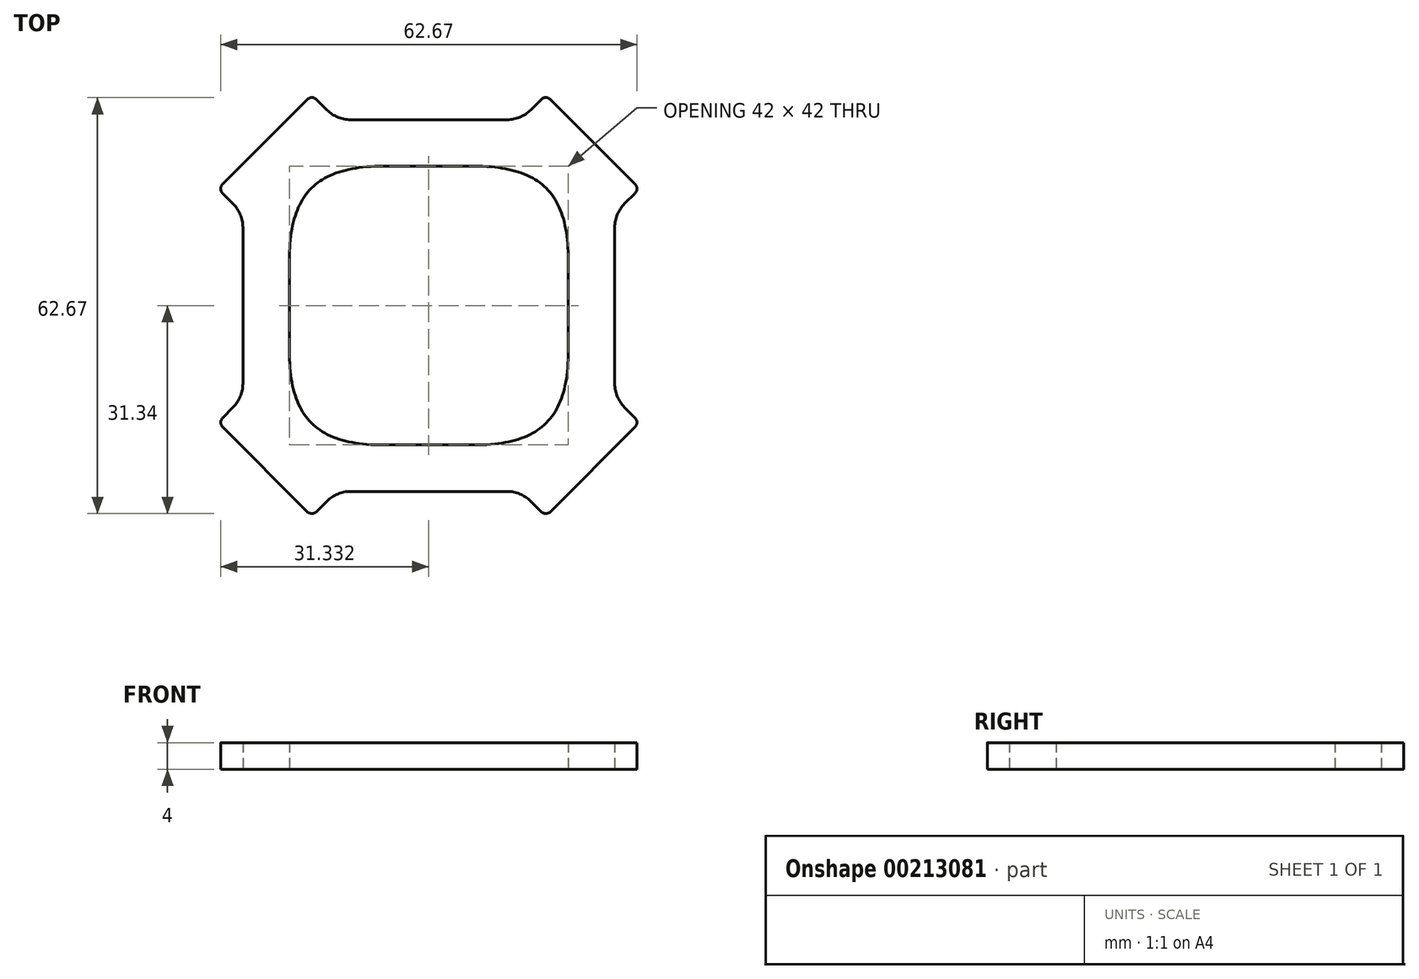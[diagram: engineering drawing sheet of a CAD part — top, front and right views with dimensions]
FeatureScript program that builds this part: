
annotation { "Feature Type Name" : "Feature", "Feature Type Description" : "" }
export const myFeature = defineFeature(function(context is Context, id is Id, definition is map)
    precondition{}
    {
        {
            var Q0;
            Q0=qCreatedBy(makeId("Top.planeOp"),FACE);
            var sketch = newSketch(context, id + "F0", { "sketchPlane" : qUnion([Q0])});
            skLineSegment(sketch, "E0", {"start": v(-155.02, 22.7) * mm, "end": v(-20.02, -112.3) * mm});
            skLineSegment(sketch, "E1", {"start": v(-155.02, -112.3) * mm, "end": v(-20.02, 22.7) * mm});
            skLineSegment(sketch, "E2", {"start": v(-104.42, -13.75) * mm, "end": v(-56.48, -61.69) * mm});
            skLineSegment(sketch, "E3", {"start": v(-118.56, -27.9) * mm, "end": v(-70.62, -75.83) * mm});
            skLineSegment(sketch, "E4", {"start": v(-118.56, -61.69) * mm, "end": v(-70.62, -13.75) * mm});
            skLineSegment(sketch, "E5", {"start": v(-104.42, -75.83) * mm, "end": v(-56.48, -27.9) * mm});
            skLineSegment(sketch, "E6", {"start": v(-115.52, -30.93) * mm, "end": v(-115.52, -58.65) * mm});
            skLineSegment(sketch, "E7", {"start": v(-59.52, -30.93) * mm, "end": v(-59.52, -58.65) * mm});
            skPoint(sketch, "E8", {"position": v(-87.52, -44.8) * mm});
            skCircle(sketch, "E9", {"center": v(-120.52, -33) * mm, "radius": 5 * mm});
            skCircle(sketch, "E10", {"center": v(-120.52, -56.58) * mm, "radius": 5 * mm});
            skCircle(sketch, "E11", {"center": v(-54.52, -33) * mm, "radius": 5 * mm});
            skCircle(sketch, "E12", {"center": v(-54.52, -56.58) * mm, "radius": 5 * mm});
            skLineSegment(sketch, "E13", {"start": v(-101.38, -16.8) * mm, "end": v(-73.66, -16.8) * mm});
            skLineSegment(sketch, "E14", {"start": v(-101.38, -72.8) * mm, "end": v(-73.66, -72.8) * mm});
            skCircle(sketch, "E15", {"center": v(-99.3, -11.8) * mm, "radius": 5 * mm});
            skCircle(sketch, "E16", {"center": v(-75.73, -11.8) * mm, "radius": 5 * mm});
            skCircle(sketch, "E17", {"center": v(-99.3, -77.8) * mm, "radius": 5 * mm});
            skCircle(sketch, "E18", {"center": v(-75.73, -77.8) * mm, "radius": 5 * mm});
            skLineSegment(sketch, "E19", {"start": v(-118.56, -26.48) * mm, "end": v(-105.83, -13.75) * mm});
            skLineSegment(sketch, "E20", {"start": v(-87.52, -30.65) * mm, "end": v(-87.52, -58.93) * mm});
            skLineSegment(sketch, "E21", {"start": v(-101.66, -44.8) * mm, "end": v(-73.38, -44.8) * mm});
            skLineSegment(sketch, "E22.MirrorCS", {"start": v(-56.48, -26.48) * mm, "end": v(-69.2, -13.75) * mm});
            skLineSegment(sketch, "E23.MirrorCS", {"start": v(-118.56, -63.1) * mm, "end": v(-105.83, -75.83) * mm});
            skLineSegment(sketch, "E24.MirrorCS", {"start": v(-56.48, -63.1) * mm, "end": v(-69.2, -75.83) * mm});
            skLineSegment(sketch, "E25", {"start": v(-94.38, -23.8) * mm, "end": v(-80.66, -23.8) * mm});
            skLineSegment(sketch, "E26", {"start": v(-108.52, -37.93) * mm, "end": v(-108.52, -51.65) * mm});
            skLineSegment(sketch, "E27.MirrorCS", {"start": v(-66.52, -37.93) * mm, "end": v(-66.52, -51.65) * mm});
            skLineSegment(sketch, "E28.MirrorCS", {"start": v(-94.38, -65.8) * mm, "end": v(-80.66, -65.8) * mm});
            skPoint(sketch, "E29.newPointB", {"position": v(-105.12, -13.04) * mm});
            skArc(sketch, "E29.filletArc", {"start": v(-104.42, -13.75) * mm, "mid": v(-105.12, -13.46) * mm, "end": v(-105.83, -13.75) * mm});
            skPoint(sketch, "E30.newPointA", {"position": v(-119.27, -27.18) * mm});
            skArc(sketch, "E30.filletArc", {"start": v(-118.56, -26.48) * mm, "mid": v(-118.85, -27.18) * mm, "end": v(-118.56, -27.9) * mm});
            skPoint(sketch, "E31.newPointB", {"position": v(-69.91, -13.04) * mm});
            skArc(sketch, "E31.filletArc", {"start": v(-69.2, -13.75) * mm, "mid": v(-69.91, -13.46) * mm, "end": v(-70.62, -13.75) * mm});
            skPoint(sketch, "E32.newPointA", {"position": v(-55.77, -27.18) * mm});
            skArc(sketch, "E32.filletArc", {"start": v(-56.48, -27.9) * mm, "mid": v(-56.18, -27.18) * mm, "end": v(-56.48, -26.48) * mm});
            skPoint(sketch, "E33.newPointB", {"position": v(-55.77, -62.4) * mm});
            skArc(sketch, "E33.filletArc", {"start": v(-56.48, -63.1) * mm, "mid": v(-56.18, -62.4) * mm, "end": v(-56.48, -61.69) * mm});
            skPoint(sketch, "E34.newPointB", {"position": v(-69.91, -76.54) * mm});
            skArc(sketch, "E34.filletArc", {"start": v(-70.62, -75.83) * mm, "mid": v(-69.91, -76.13) * mm, "end": v(-69.2, -75.83) * mm});
            skPoint(sketch, "E35.newPointB", {"position": v(-105.12, -76.54) * mm});
            skArc(sketch, "E35.filletArc", {"start": v(-105.83, -75.83) * mm, "mid": v(-105.12, -76.13) * mm, "end": v(-104.42, -75.83) * mm});
            skPoint(sketch, "E36.newPointA", {"position": v(-119.27, -62.4) * mm});
            skArc(sketch, "E36.filletArc", {"start": v(-118.56, -61.69) * mm, "mid": v(-118.85, -62.4) * mm, "end": v(-118.56, -63.1) * mm});
            skPoint(sketch, "E37.visualSharp", {"position": v(-108.52, -51.65) * mm});
            skPoint(sketch, "E38.visualSharp", {"position": v(-94.38, -65.8) * mm});
            skPoint(sketch, "E39.visualSharp", {"position": v(-80.66, -65.8) * mm});
            skPoint(sketch, "E40.visualSharp", {"position": v(-66.52, -51.65) * mm});
            skPoint(sketch, "E41.visualSharp", {"position": v(-66.52, -37.93) * mm});
            skPoint(sketch, "E42.visualSharp", {"position": v(-80.66, -23.8) * mm});
            skPoint(sketch, "E43.visualSharp", {"position": v(-94.38, -23.8) * mm});
            skPoint(sketch, "E44.visualSharp", {"position": v(-108.52, -37.93) * mm});
            skFitSpline(sketch, "E45", {"points": [v(-108.52, -37.93) * mm, v(-94.38, -23.8) * mm], "startDerivative": vector(0, 30) * mm, "endDerivative": vector(30, 0) * mm});
            skFitSpline(sketch, "E46", {"points": [v(-80.66, -23.8) * mm, v(-66.52, -37.93) * mm], "startDerivative": vector(30, 0) * mm, "endDerivative": vector(0, -30) * mm});
            skFitSpline(sketch, "E47.MirrorCS", {"points": [v(-108.52, -51.65) * mm, v(-94.38, -65.8) * mm], "startDerivative": vector(0, -30) * mm, "endDerivative": vector(30, 0) * mm});
            skFitSpline(sketch, "E48.MirrorCS", {"points": [v(-80.66, -65.8) * mm, v(-66.52, -51.65) * mm], "startDerivative": vector(30, 0) * mm, "endDerivative": vector(0, 30) * mm});
            skPoint(sketch, "E49.centerSnap0", {"position": v(-108.52, -44.8) * mm});
            skSolve(sketch);
        }
        {
            var Q0;
            {var subQ0=sQuery(id+"F0.wireOp",EDGE,"E6");Q0=makeQuery(id+"F0.imprint","IMPRINT",FACE,{"disambiguationData":[TD([[makeQuery(id+"F0.imprint","IMPRINT",EDGE,{"derivedFrom":subQ0}),1.0]])]});}
            var Q1;
            {var subQ0=sQuery(id+"F0.wireOp",EDGE,"E4");var subQ1=sQuery(id+"F0.wireOp",EDGE,"IkjAp8gk-rOio-6rVX-yXqz-ps8Z3xEeHPRW");var subQ2=makeQuery(id+"F0.imprint","INTERSECT",VERTEX,{"derivedFrom":[subQ1,subQ0]});Q1=makeQuery(id+"F0.imprint","IMPRINT",FACE,{"disambiguationData":[TD([[makeQuery(id+"F0.imprint","IMPRINT",EDGE,{"disambiguationData":[TD([[subQ2,1.0]])],"derivedFrom":subQ1}),-1.0]])]});}
            var Q2;
            {var subQ0=sQuery(id+"F0.wireOp",EDGE,"E5");var subQ1=sQuery(id+"F0.wireOp",EDGE,"IkjAp8gk-rOio-6rVX-yXqz-ps8Z3xEeHPRW");var subQ2=makeQuery(id+"F0.imprint","INTERSECT",VERTEX,{"derivedFrom":[subQ1,subQ0]});Q2=makeQuery(id+"F0.imprint","IMPRINT",FACE,{"disambiguationData":[TD([[makeQuery(id+"F0.imprint","IMPRINT",EDGE,{"disambiguationData":[TD([[subQ2,-1.0]])],"derivedFrom":subQ1}),-1.0]])]});}
            var Q3;
            {var subQ0=sQuery(id+"F0.wireOp",EDGE,"E3");var subQ1=sQuery(id+"F0.wireOp",EDGE,"iNsC8I3S-PSnE-EiiR-C7q5-jpwtKowtfSVf");var subQ2=makeQuery(id+"F0.imprint","INTERSECT",VERTEX,{"derivedFrom":[subQ1,subQ0]});Q3=makeQuery(id+"F0.imprint","IMPRINT",FACE,{"disambiguationData":[TD([[makeQuery(id+"F0.imprint","IMPRINT",EDGE,{"disambiguationData":[TD([[subQ2,1.0]])],"derivedFrom":subQ1}),-1.0]])]});}
            var Q4;
            {var subQ0=sQuery(id+"F0.wireOp",EDGE,"E2");var subQ1=sQuery(id+"F0.wireOp",EDGE,"iNsC8I3S-PSnE-EiiR-C7q5-jpwtKowtfSVf");var subQ2=makeQuery(id+"F0.imprint","INTERSECT",VERTEX,{"derivedFrom":[subQ1,subQ0]});Q4=makeQuery(id+"F0.imprint","IMPRINT",FACE,{"disambiguationData":[TD([[makeQuery(id+"F0.imprint","IMPRINT",EDGE,{"disambiguationData":[TD([[subQ2,-1.0]])],"derivedFrom":subQ1}),-1.0]])]});}
            var Q5;
            {var subQ0=sQuery(id+"F0.wireOp",EDGE,"E4");var subQ1=sQuery(id+"F0.wireOp",EDGE,"60YYQdTG-lnKG-K1mv-Ih9S-ZKM6xGfFZAeJ");var subQ2=makeQuery(id+"F0.imprint","INTERSECT",VERTEX,{"derivedFrom":[subQ1,subQ0]});Q5=makeQuery(id+"F0.imprint","IMPRINT",FACE,{"disambiguationData":[TD([[makeQuery(id+"F0.imprint","IMPRINT",EDGE,{"disambiguationData":[TD([[subQ2,-1.0]])],"derivedFrom":subQ1}),-1.0]])]});}
            var Q6;
            {var subQ0=sQuery(id+"F0.wireOp",EDGE,"E5");var subQ1=sQuery(id+"F0.wireOp",EDGE,"60YYQdTG-lnKG-K1mv-Ih9S-ZKM6xGfFZAeJ");var subQ2=makeQuery(id+"F0.imprint","INTERSECT",VERTEX,{"derivedFrom":[subQ1,subQ0]});Q6=makeQuery(id+"F0.imprint","IMPRINT",FACE,{"disambiguationData":[TD([[makeQuery(id+"F0.imprint","IMPRINT",EDGE,{"disambiguationData":[TD([[subQ2,1.0]])],"derivedFrom":subQ1}),-1.0]])]});}
            var Q7;
            {var subQ0=sQuery(id+"F0.wireOp",EDGE,"E2");var subQ1=sQuery(id+"F0.wireOp",EDGE,"55MOo5qS-ibKR-kUwh-Ymrc-RgTBuaNrgUC7");var subQ2=makeQuery(id+"F0.imprint","INTERSECT",VERTEX,{"derivedFrom":[subQ1,subQ0]});Q7=makeQuery(id+"F0.imprint","IMPRINT",FACE,{"disambiguationData":[TD([[makeQuery(id+"F0.imprint","IMPRINT",EDGE,{"disambiguationData":[TD([[subQ2,1.0]])],"derivedFrom":subQ1}),-1.0]])]});}
            var Q8;
            {var subQ0=sQuery(id+"F0.wireOp",EDGE,"E3");var subQ1=sQuery(id+"F0.wireOp",EDGE,"55MOo5qS-ibKR-kUwh-Ymrc-RgTBuaNrgUC7");var subQ2=makeQuery(id+"F0.imprint","INTERSECT",VERTEX,{"derivedFrom":[subQ1,subQ0]});Q8=makeQuery(id+"F0.imprint","IMPRINT",FACE,{"disambiguationData":[TD([[makeQuery(id+"F0.imprint","IMPRINT",EDGE,{"disambiguationData":[TD([[subQ2,-1.0]])],"derivedFrom":subQ1}),-1.0]])]});}
            var Q9;
            {var subQ0=sQuery(id+"F0.wireOp",EDGE,"IkjAp8gk-rOio-6rVX-yXqz-ps8Z3xEeHPRW");var subQ4=makeQuery(id+"F0.imprint","INTERSECT",VERTEX,{"derivedFrom":[subQ0,sQuery(id+"F0.wireOp",EDGE,"E4")]});Q9=makeQuery(id+"F0.imprint","IMPRINT",FACE,{"disambiguationData":[TD([[makeQuery(id+"F0.imprint","IMPRINT",EDGE,{"disambiguationData":[TD([[subQ4,1.0]])],"derivedFrom":subQ0}),1.0]])]});}
            var Q10;
            {var subQ0=sQuery(id+"F0.wireOp",EDGE,"E4");var subQ6=sQuery(id+"F0.wireOp",EDGE,"IkjAp8gk-rOio-6rVX-yXqz-ps8Z3xEeHPRW");var subQ8=makeQuery(id+"F0.imprint","INTERSECT",VERTEX,{"derivedFrom":[subQ6,subQ0]});Q10=makeQuery(id+"F0.imprint","IMPRINT",FACE,{"disambiguationData":[TD([[makeQuery(id+"F0.imprint","IMPRINT",EDGE,{"disambiguationData":[TD([[subQ8,-1.0]])],"derivedFrom":subQ6}),-1.0]])]});}
            var Q11;
            {var subQ0=sQuery(id+"F0.wireOp",EDGE,"iNsC8I3S-PSnE-EiiR-C7q5-jpwtKowtfSVf");var subQ4=makeQuery(id+"F0.imprint","INTERSECT",VERTEX,{"derivedFrom":[subQ0,sQuery(id+"F0.wireOp",EDGE,"tVrrdReX-4nvy-7fY8-IXP5-rTPEuiRywHbx")]});Q11=makeQuery(id+"F0.imprint","IMPRINT",FACE,{"disambiguationData":[TD([[makeQuery(id+"F0.imprint","IMPRINT",EDGE,{"disambiguationData":[TD([[subQ4,1.0]])],"derivedFrom":subQ0}),1.0]])]});}
            var Q12;
            {var subQ0=sQuery(id+"F0.wireOp",EDGE,"E2");var subQ4=sQuery(id+"F0.wireOp",EDGE,"iNsC8I3S-PSnE-EiiR-C7q5-jpwtKowtfSVf");var subQ5=makeQuery(id+"F0.imprint","INTERSECT",VERTEX,{"derivedFrom":[subQ4,subQ0]});Q12=makeQuery(id+"F0.imprint","IMPRINT",FACE,{"disambiguationData":[TD([[makeQuery(id+"F0.imprint","IMPRINT",EDGE,{"disambiguationData":[TD([[subQ5,1.0]])],"derivedFrom":subQ4}),-1.0]])]});}
            var Q13;
            {var subQ0=sQuery(id+"F0.wireOp",EDGE,"60YYQdTG-lnKG-K1mv-Ih9S-ZKM6xGfFZAeJ");var subQ5=makeQuery(id+"F0.imprint","INTERSECT",VERTEX,{"derivedFrom":[subQ0,sQuery(id+"F0.wireOp",EDGE,"E5")]});Q13=makeQuery(id+"F0.imprint","IMPRINT",FACE,{"disambiguationData":[TD([[makeQuery(id+"F0.imprint","IMPRINT",EDGE,{"disambiguationData":[TD([[subQ5,-1.0]])],"derivedFrom":subQ0}),1.0]])]});}
            var Q14;
            {var subQ0=sQuery(id+"F0.wireOp",EDGE,"E5");var subQ1=sQuery(id+"F0.wireOp",EDGE,"60YYQdTG-lnKG-K1mv-Ih9S-ZKM6xGfFZAeJ");var subQ2=makeQuery(id+"F0.imprint","INTERSECT",VERTEX,{"derivedFrom":[subQ1,subQ0]});Q14=makeQuery(id+"F0.imprint","IMPRINT",FACE,{"disambiguationData":[TD([[makeQuery(id+"F0.imprint","IMPRINT",EDGE,{"disambiguationData":[TD([[subQ2,-1.0]])],"derivedFrom":subQ1}),-1.0]])]});}
            var Q15;
            {var subQ0=sQuery(id+"F0.wireOp",EDGE,"55MOo5qS-ibKR-kUwh-Ymrc-RgTBuaNrgUC7");var subQ4=makeQuery(id+"F0.imprint","INTERSECT",VERTEX,{"derivedFrom":[subQ0,sQuery(id+"F0.wireOp",EDGE,"E2")]});Q15=makeQuery(id+"F0.imprint","IMPRINT",FACE,{"disambiguationData":[TD([[makeQuery(id+"F0.imprint","IMPRINT",EDGE,{"disambiguationData":[TD([[subQ4,1.0]])],"derivedFrom":subQ0}),1.0]])]});}
            var Q16;
            {var subQ0=sQuery(id+"F0.wireOp",EDGE,"E3");var subQ1=sQuery(id+"F0.wireOp",EDGE,"55MOo5qS-ibKR-kUwh-Ymrc-RgTBuaNrgUC7");var subQ2=makeQuery(id+"F0.imprint","INTERSECT",VERTEX,{"derivedFrom":[subQ1,subQ0]});Q16=makeQuery(id+"F0.imprint","IMPRINT",FACE,{"disambiguationData":[TD([[makeQuery(id+"F0.imprint","IMPRINT",EDGE,{"disambiguationData":[TD([[subQ2,1.0]])],"derivedFrom":subQ1}),-1.0]])]});}
            var Q17;
            {var subQ3=sQuery(id+"F0.wireOp",EDGE,"E5");var subQ5=sQuery(id+"F0.wireOp",EDGE,"IkjAp8gk-rOio-6rVX-yXqz-ps8Z3xEeHPRW");var subQ8=makeQuery(id+"F0.imprint","INTERSECT",VERTEX,{"derivedFrom":[subQ5,subQ3]});Q17=makeQuery(id+"F0.imprint","IMPRINT",FACE,{"disambiguationData":[TD([[makeQuery(id+"F0.imprint","IMPRINT",EDGE,{"disambiguationData":[TD([[subQ8,1.0]])],"derivedFrom":subQ5}),-1.0]])]});}
            var Q18;
            {var subQ0=sQuery(id+"F0.wireOp",EDGE,"E3");var subQ3=sQuery(id+"F0.wireOp",EDGE,"iNsC8I3S-PSnE-EiiR-C7q5-jpwtKowtfSVf");var subQ4=makeQuery(id+"F0.imprint","INTERSECT",VERTEX,{"derivedFrom":[subQ3,subQ0]});Q18=makeQuery(id+"F0.imprint","IMPRINT",FACE,{"disambiguationData":[TD([[makeQuery(id+"F0.imprint","IMPRINT",EDGE,{"disambiguationData":[TD([[subQ4,-1.0]])],"derivedFrom":subQ3}),-1.0]])]});}
            var Q19;
            {var subQ0=sQuery(id+"F0.wireOp",EDGE,"E2");var subQ4=sQuery(id+"F0.wireOp",EDGE,"55MOo5qS-ibKR-kUwh-Ymrc-RgTBuaNrgUC7");var subQ9=makeQuery(id+"F0.imprint","INTERSECT",VERTEX,{"derivedFrom":[subQ4,subQ0]});Q19=makeQuery(id+"F0.imprint","IMPRINT",FACE,{"disambiguationData":[TD([[makeQuery(id+"F0.imprint","IMPRINT",EDGE,{"disambiguationData":[TD([[subQ9,-1.0]])],"derivedFrom":subQ4}),-1.0]])]});}
            var Q20;
            {var subQ0=sQuery(id+"F0.wireOp",EDGE,"E6");var subQ1=sQuery(id+"F0.wireOp",EDGE,"E3");var subQ2=makeQuery(id+"F0.imprint","INTERSECT",VERTEX,{"derivedFrom":[subQ1,subQ0]});Q20=makeQuery(id+"F0.imprint","IMPRINT",FACE,{"disambiguationData":[TD([[makeQuery(id+"F0.imprint","IMPRINT",EDGE,{"disambiguationData":[TD([[subQ2,1.0]])],"derivedFrom":subQ1}),-1.0]])]});}
            var Q21;
            {var subQ0=sQuery(id+"F0.wireOp",EDGE,"E7");var subQ1=sQuery(id+"F0.wireOp",EDGE,"E5");var subQ2=makeQuery(id+"F0.imprint","INTERSECT",VERTEX,{"derivedFrom":[subQ1,subQ0]});Q21=makeQuery(id+"F0.imprint","IMPRINT",FACE,{"disambiguationData":[TD([[makeQuery(id+"F0.imprint","IMPRINT",EDGE,{"disambiguationData":[TD([[subQ2,-1.0]])],"derivedFrom":subQ1}),-1.0]])]});}
            var Q22;
            {var subQ0=sQuery(id+"F0.wireOp",EDGE,"E7");var subQ5=sQuery(id+"F0.wireOp",EDGE,"E2");var subQ7=makeQuery(id+"F0.imprint","INTERSECT",VERTEX,{"derivedFrom":[subQ5,subQ0]});Q22=makeQuery(id+"F0.imprint","IMPRINT",FACE,{"disambiguationData":[TD([[makeQuery(id+"F0.imprint","IMPRINT",EDGE,{"disambiguationData":[TD([[subQ7,1.0]])],"derivedFrom":subQ5}),1.0]])]});}
            var Q23;
            {var subQ0=sQuery(id+"F0.wireOp",EDGE,"E7");var subQ1=sQuery(id+"F0.wireOp",EDGE,"E2");var subQ2=makeQuery(id+"F0.imprint","INTERSECT",VERTEX,{"derivedFrom":[subQ1,subQ0]});Q23=makeQuery(id+"F0.imprint","IMPRINT",FACE,{"disambiguationData":[TD([[makeQuery(id+"F0.imprint","IMPRINT",EDGE,{"disambiguationData":[TD([[subQ2,-1.0]])],"derivedFrom":subQ1}),1.0]])]});}
            var Q24;
            {var subQ0=sQuery(id+"F0.wireOp",EDGE,"E6");var subQ1=sQuery(id+"F0.wireOp",EDGE,"E4");var subQ2=makeQuery(id+"F0.imprint","INTERSECT",VERTEX,{"derivedFrom":[subQ1,subQ0]});Q24=makeQuery(id+"F0.imprint","IMPRINT",FACE,{"disambiguationData":[TD([[makeQuery(id+"F0.imprint","IMPRINT",EDGE,{"disambiguationData":[TD([[subQ2,1.0]])],"derivedFrom":subQ1}),1.0]])]});}
            var Q25;
            {var subQ0=sQuery(id+"F0.wireOp",EDGE,"E4");var subQ1=sQuery(id+"F0.wireOp",EDGE,"60YYQdTG-lnKG-K1mv-Ih9S-ZKM6xGfFZAeJ");var subQ2=makeQuery(id+"F0.imprint","INTERSECT",VERTEX,{"derivedFrom":[subQ1,subQ0]});Q25=makeQuery(id+"F0.imprint","IMPRINT",FACE,{"disambiguationData":[TD([[makeQuery(id+"F0.imprint","IMPRINT",EDGE,{"disambiguationData":[TD([[subQ2,1.0]])],"derivedFrom":subQ1}),-1.0]])]});}
            var Q26;
            {var subQ0=sQuery(id+"F0.wireOp",EDGE,"E13");var subQ3=sQuery(id+"F0.wireOp",EDGE,"E2");var subQ4=makeQuery(id+"F0.imprint","INTERSECT",VERTEX,{"derivedFrom":[subQ3,subQ0]});Q26=makeQuery(id+"F0.imprint","IMPRINT",FACE,{"disambiguationData":[TD([[makeQuery(id+"F0.imprint","IMPRINT",EDGE,{"disambiguationData":[TD([[subQ4,-1.0]])],"derivedFrom":subQ3}),1.0]])]});}
            var Q27;
            {var subQ0=sQuery(id+"F0.wireOp",EDGE,"E13");var subQ1=sQuery(id+"F0.wireOp",EDGE,"E2");var subQ2=makeQuery(id+"F0.imprint","INTERSECT",VERTEX,{"derivedFrom":[subQ1,subQ0]});Q27=makeQuery(id+"F0.imprint","IMPRINT",FACE,{"disambiguationData":[TD([[makeQuery(id+"F0.imprint","IMPRINT",EDGE,{"disambiguationData":[TD([[subQ2,1.0]])],"derivedFrom":subQ1}),1.0]])]});}
            var Q28;
            {var subQ0=sQuery(id+"F0.wireOp",EDGE,"E13");var subQ1=sQuery(id+"F0.wireOp",EDGE,"E4");var subQ2=makeQuery(id+"F0.imprint","INTERSECT",VERTEX,{"derivedFrom":[subQ1,subQ0]});Q28=makeQuery(id+"F0.imprint","IMPRINT",FACE,{"disambiguationData":[TD([[makeQuery(id+"F0.imprint","IMPRINT",EDGE,{"disambiguationData":[TD([[subQ2,-1.0]])],"derivedFrom":subQ1}),1.0]])]});}
            var Q29;
            {var subQ0=sQuery(id+"F0.wireOp",EDGE,"E14");var subQ5=sQuery(id+"F0.wireOp",EDGE,"E3");var subQ7=makeQuery(id+"F0.imprint","INTERSECT",VERTEX,{"derivedFrom":[subQ5,subQ0]});Q29=makeQuery(id+"F0.imprint","IMPRINT",FACE,{"disambiguationData":[TD([[makeQuery(id+"F0.imprint","IMPRINT",EDGE,{"disambiguationData":[TD([[subQ7,1.0]])],"derivedFrom":subQ5}),-1.0]])]});}
            var Q30;
            {var subQ0=sQuery(id+"F0.wireOp",EDGE,"E14");var subQ1=sQuery(id+"F0.wireOp",EDGE,"E5");var subQ2=makeQuery(id+"F0.imprint","INTERSECT",VERTEX,{"derivedFrom":[subQ1,subQ0]});Q30=makeQuery(id+"F0.imprint","IMPRINT",FACE,{"disambiguationData":[TD([[makeQuery(id+"F0.imprint","IMPRINT",EDGE,{"disambiguationData":[TD([[subQ2,1.0]])],"derivedFrom":subQ1}),-1.0]])]});}
            var Q31;
            {var subQ0=sQuery(id+"F0.wireOp",EDGE,"E14");var subQ1=sQuery(id+"F0.wireOp",EDGE,"E3");var subQ2=makeQuery(id+"F0.imprint","INTERSECT",VERTEX,{"derivedFrom":[subQ1,subQ0]});Q31=makeQuery(id+"F0.imprint","IMPRINT",FACE,{"disambiguationData":[TD([[makeQuery(id+"F0.imprint","IMPRINT",EDGE,{"disambiguationData":[TD([[subQ2,-1.0]])],"derivedFrom":subQ1}),-1.0]])]});}
            var Q32;
            {var subQ4=sQuery(id+"F0.wireOp",EDGE,"E19");var subQ7=sQuery(id+"F0.wireOp",EDGE,"E0");var subQ8=makeQuery(id+"F0.imprint","INTERSECT",VERTEX,{"derivedFrom":[subQ7,subQ4]});Q32=makeQuery(id+"F0.imprint","IMPRINT",FACE,{"disambiguationData":[TD([[makeQuery(id+"F0.imprint","IMPRINT",EDGE,{"disambiguationData":[TD([[subQ8,-1.0]])],"derivedFrom":subQ7}),-1.0]])]});}
            var Q33;
            {var subQ5=sQuery(id+"F0.wireOp",EDGE,"E19");var subQ7=sQuery(id+"F0.wireOp",EDGE,"E0");var subQ8=makeQuery(id+"F0.imprint","INTERSECT",VERTEX,{"derivedFrom":[subQ7,subQ5]});Q33=makeQuery(id+"F0.imprint","IMPRINT",FACE,{"disambiguationData":[TD([[makeQuery(id+"F0.imprint","IMPRINT",EDGE,{"disambiguationData":[TD([[subQ8,-1.0]])],"derivedFrom":subQ7}),1.0]])]});}
            var Q34;
            {var subQ4=sQuery(id+"F0.wireOp",EDGE,"E22.MirrorCS");var subQ7=sQuery(id+"F0.wireOp",EDGE,"E1");var subQ8=makeQuery(id+"F0.imprint","INTERSECT",VERTEX,{"derivedFrom":[subQ7,subQ4]});Q34=makeQuery(id+"F0.imprint","IMPRINT",FACE,{"disambiguationData":[TD([[makeQuery(id+"F0.imprint","IMPRINT",EDGE,{"disambiguationData":[TD([[subQ8,1.0]])],"derivedFrom":subQ7}),1.0]])]});}
            var Q35;
            {var subQ0=sQuery(id+"F0.wireOp",EDGE,"E22.MirrorCS");var subQ7=sQuery(id+"F0.wireOp",EDGE,"E1");var subQ8=makeQuery(id+"F0.imprint","INTERSECT",VERTEX,{"derivedFrom":[subQ7,subQ0]});Q35=makeQuery(id+"F0.imprint","IMPRINT",FACE,{"disambiguationData":[TD([[makeQuery(id+"F0.imprint","IMPRINT",EDGE,{"disambiguationData":[TD([[subQ8,1.0]])],"derivedFrom":subQ7}),-1.0]])]});}
            var Q36;
            {var subQ0=sQuery(id+"F0.wireOp",EDGE,"E24.MirrorCS");var subQ4=sQuery(id+"F0.wireOp",EDGE,"E0");var subQ5=makeQuery(id+"F0.imprint","INTERSECT",VERTEX,{"derivedFrom":[subQ4,subQ0]});Q36=makeQuery(id+"F0.imprint","IMPRINT",FACE,{"disambiguationData":[TD([[makeQuery(id+"F0.imprint","IMPRINT",EDGE,{"disambiguationData":[TD([[subQ5,1.0]])],"derivedFrom":subQ4}),1.0]])]});}
            var Q37;
            {var subQ0=sQuery(id+"F0.wireOp",EDGE,"E24.MirrorCS");var subQ7=sQuery(id+"F0.wireOp",EDGE,"E0");var subQ8=makeQuery(id+"F0.imprint","INTERSECT",VERTEX,{"derivedFrom":[subQ7,subQ0]});Q37=makeQuery(id+"F0.imprint","IMPRINT",FACE,{"disambiguationData":[TD([[makeQuery(id+"F0.imprint","IMPRINT",EDGE,{"disambiguationData":[TD([[subQ8,1.0]])],"derivedFrom":subQ7}),-1.0]])]});}
            var Q38;
            {var subQ4=sQuery(id+"F0.wireOp",EDGE,"E23.MirrorCS");var subQ5=sQuery(id+"F0.wireOp",EDGE,"E1");var subQ6=makeQuery(id+"F0.imprint","INTERSECT",VERTEX,{"derivedFrom":[subQ5,subQ4]});Q38=makeQuery(id+"F0.imprint","IMPRINT",FACE,{"disambiguationData":[TD([[makeQuery(id+"F0.imprint","IMPRINT",EDGE,{"disambiguationData":[TD([[subQ6,-1.0]])],"derivedFrom":subQ5}),-1.0]])]});}
            var Q39;
            {var subQ3=sQuery(id+"F0.wireOp",EDGE,"E23.MirrorCS");var subQ7=sQuery(id+"F0.wireOp",EDGE,"E1");var subQ8=makeQuery(id+"F0.imprint","INTERSECT",VERTEX,{"derivedFrom":[subQ7,subQ3]});Q39=makeQuery(id+"F0.imprint","IMPRINT",FACE,{"disambiguationData":[TD([[makeQuery(id+"F0.imprint","IMPRINT",EDGE,{"disambiguationData":[TD([[subQ8,-1.0]])],"derivedFrom":subQ7}),1.0]])]});}
            extrude(context, id + "F1", {"entities" : qUnion([Q0, Q1, Q2, Q3, Q4, Q5, Q6, Q7, Q8, Q9, Q10, Q11, Q12, Q13, Q14, Q15, Q16, Q17, Q18, Q19, Q20, Q21, Q22, Q23, Q24, Q25, Q26, Q27, Q28, Q29, Q30, Q31, Q32, Q33, Q34, Q35, Q36, Q37, Q38, Q39]), "depth" : 4 * mm});
        }
    });
